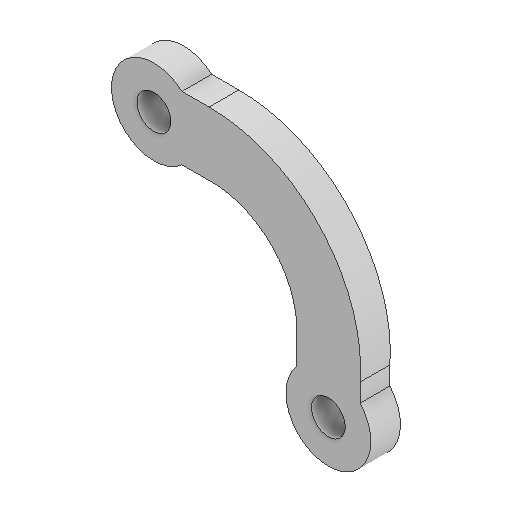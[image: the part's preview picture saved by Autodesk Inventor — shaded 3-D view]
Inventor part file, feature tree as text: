
AUTODESK INVENTOR PART (.ipt)
format: ipt  version: 2025 (Build 290162010, 162A)  size: 114,176 bytes
history: native  units: in
note: dims shown in document units (in); Inventor stores cm internally (conversion verified against a paired STEP export)
features: extrude x1, sketch x1
ambient origin geometry x8: Origin, YZ Plane, XZ Plane, XY Plane, X Axis, Y Axis, Z Axis, Center Point
bodies: Solid1 (feature_tree)
feature tree (2):
  extrude  "Extrusion1"  Depth=0.14in
  sketch  "Sketch1"  dims[d0=0.16in d1=0.4in d2=0.3in d3=0.15in d4=0.16in d5=0.4in d6=0.3in d7=0.15in d8=0.14in d9=0.0in]
